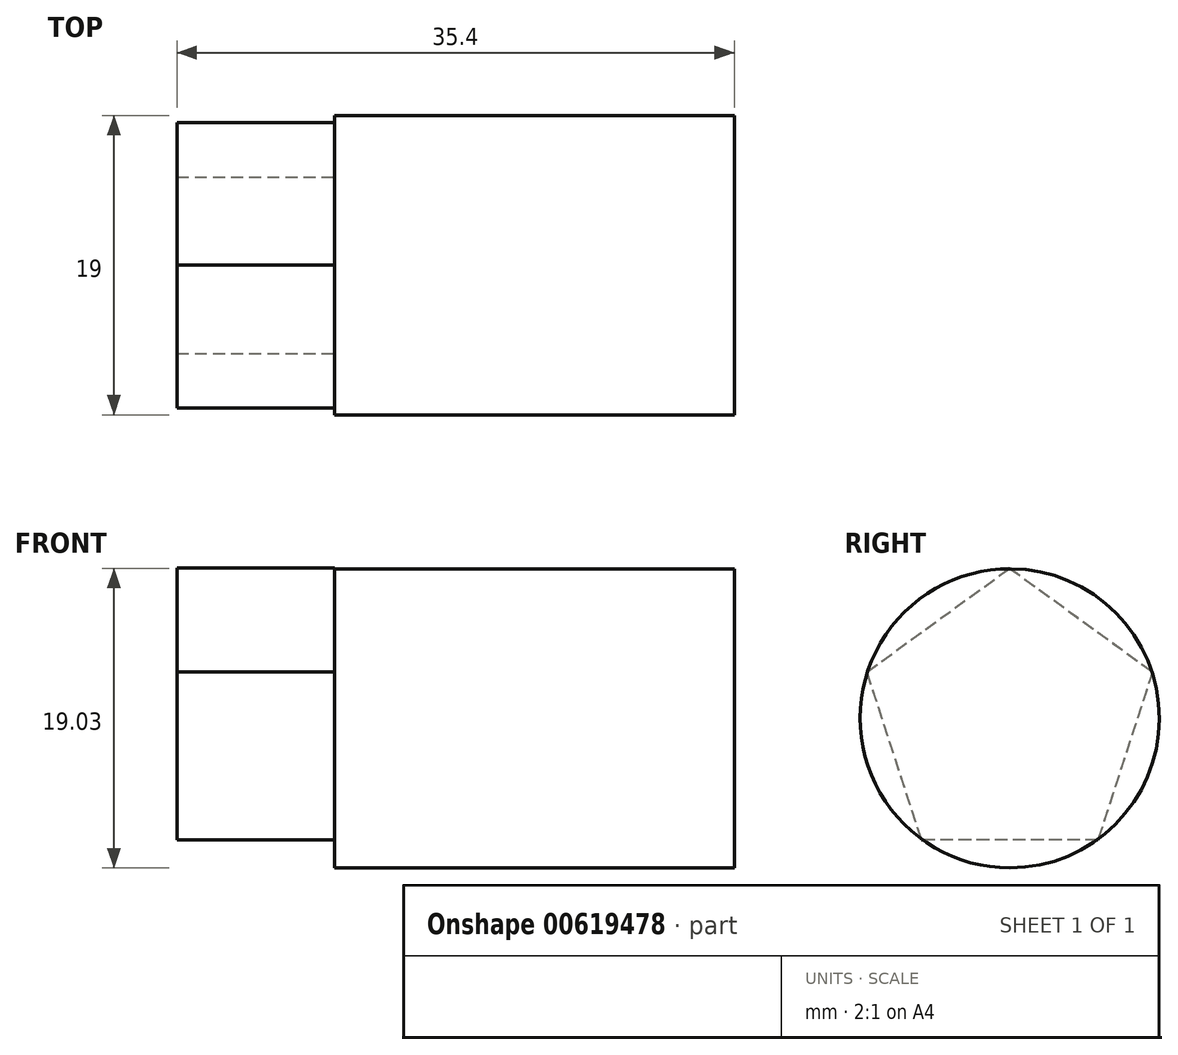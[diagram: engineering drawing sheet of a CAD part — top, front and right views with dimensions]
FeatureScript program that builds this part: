
annotation { "Feature Type Name" : "Feature", "Feature Type Description" : "" }
export const myFeature = defineFeature(function(context is Context, id is Id, definition is map)
    precondition{}
    {
        {
            var Q0;
            Q0=qCreatedBy(makeId("Right.planeOp"),FACE);
            var sketch = newSketch(context, id + "F0", { "sketchPlane" : qUnion([Q0])});
            skCircle(sketch, "E0", {"center": v(0, 0) * mm, "radius": 9.5 * mm});
            skSolve(sketch);
        }
        {
            var Q0;
            Q0=qCreatedBy(makeId("Right.planeOp"),FACE);
            var sketch = newSketch(context, id + "F1", { "sketchPlane" : qUnion([Q0])});
            skCircle(sketch, "E1.cCircle", {"center": v(0, 0) * mm, "radius": 9.53 * mm, "construction": true});
            skLineSegment(sketch, "E1.0", {"start": v(0, 9.53) * mm, "end": v(9.07, 2.95) * mm});
            skLineSegment(sketch, "E1.1", {"start": v(9.07, 2.95) * mm, "end": v(5.6, -7.71) * mm});
            skLineSegment(sketch, "E1.2", {"start": v(5.6, -7.71) * mm, "end": v(-5.6, -7.71) * mm});
            skLineSegment(sketch, "E1.3", {"start": v(-5.6, -7.71) * mm, "end": v(-9.07, 2.95) * mm});
            skLineSegment(sketch, "E1.4", {"start": v(-9.07, 2.95) * mm, "end": v(0, 9.53) * mm});
            skSolve(sketch);
        }
        {
            var Q0;
            Q0=makeQuery(id+"F0.imprint","IMPRINT",FACE,{"disambiguationData":[TD([[makeQuery(id+"F0.imprint","IMPRINT",EDGE,{"derivedFrom":sQuery(id+"F0.wireOp",EDGE,"E0")}),1.0]])]});
            extrude(context, id + "F2", {"entities" : qUnion([Q0]), "depth" : 25.4 * mm, "offsetDistance" : 25.4 * mm});
        }
        {
            var Q0;
            Q0=makeQuery(id+"F1.imprint","IMPRINT",FACE,{"disambiguationData":[TD([[makeQuery(id+"F1.imprint","IMPRINT",EDGE,{"derivedFrom":sQuery(id+"F1.wireOp",EDGE,"E1.0")}),-1.0]])]});
            extrude(context, id + "F3", {"entities" : qUnion([Q0]), "operationType" : NewBodyOperationType.ADD, "oppositeDirection" : true, "depth" : 10 * mm, "offsetDistance" : 25.4 * mm});
        }
    });
